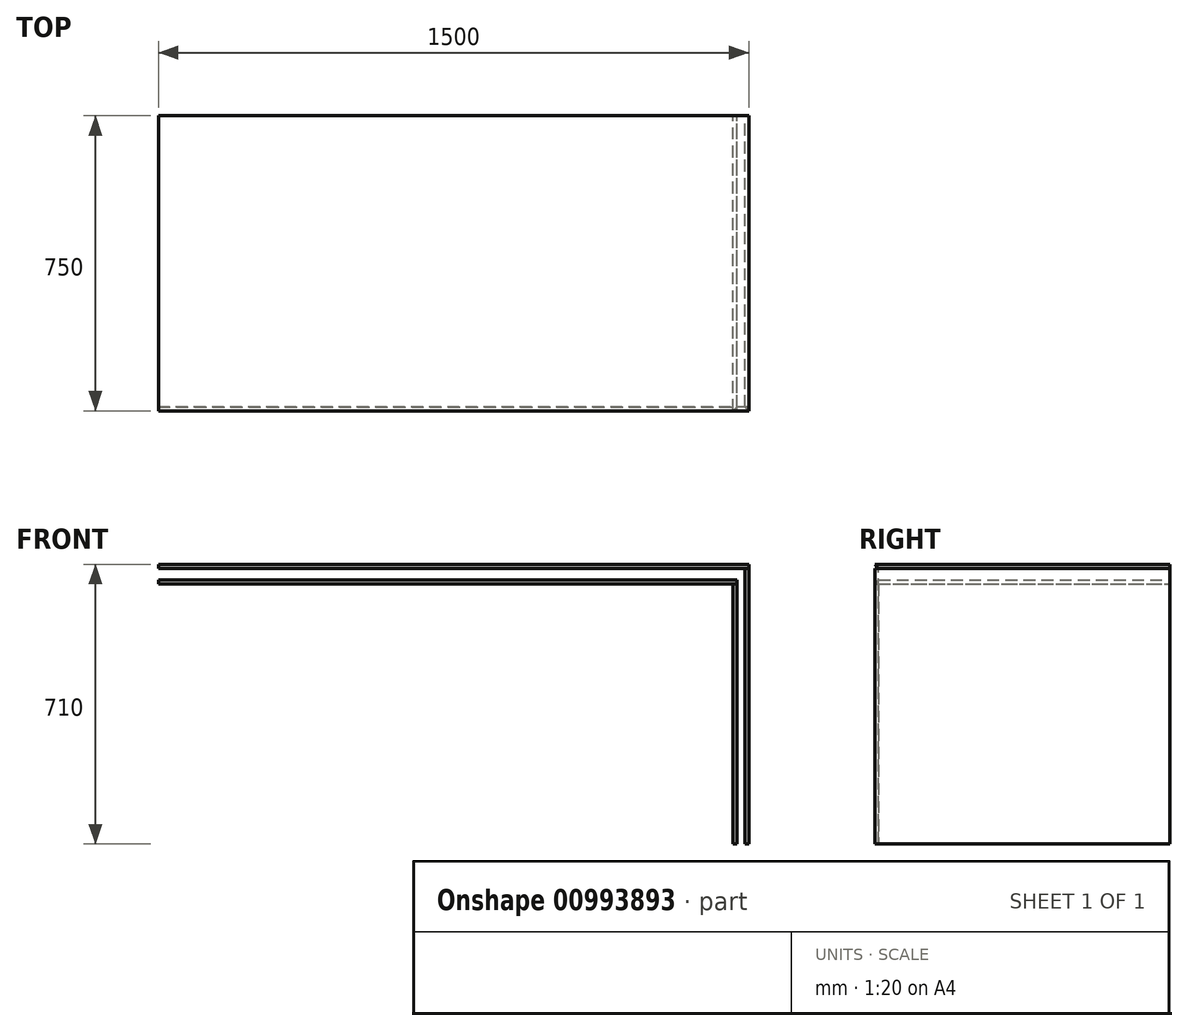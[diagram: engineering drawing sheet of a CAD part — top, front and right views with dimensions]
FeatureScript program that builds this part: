
annotation { "Feature Type Name" : "Feature", "Feature Type Description" : "" }
export const myFeature = defineFeature(function(context is Context, id is Id, definition is map)
    precondition{}
    {
        {
            assignVariable(context, id + "F0", {"name" : "t_board_thickness", "anyValue" : 10});
        }
        {
            assignVariable(context, id + "F1", {"name" : "t_depth", "anyValue" : 750});
        }
        {
            var Q0;
            Q0=qCreatedBy(makeId("Front.planeOp"),FACE);
            var sketch = newSketch(context, id + "F2", { "sketchPlane" : qUnion([Q0])});
            skLineSegment(sketch, "E0.bottom", {"start": v(-1265, 2470) * mm, "end": v(1265, 2470) * mm});
            skLineSegment(sketch, "E0.top", {"start": v(-1265, 0) * mm, "end": v(1265, 0) * mm});
            skLineSegment(sketch, "E0.left", {"start": v(-1265, 2470) * mm, "end": v(-1265, 0) * mm});
            skLineSegment(sketch, "E0.right", {"start": v(1265, 2470) * mm, "end": v(1265, 0) * mm});
            skSolve(sketch);
        }
        {
            var Q0;
            Q0=makeQuery(id+"F2.imprint","IMPRINT",FACE,{"disambiguationData":[TD([[makeQuery(id+"F2.imprint","IMPRINT",EDGE,{"derivedFrom":sQuery(id+"F2.wireOp",EDGE,"E0.bottom")}),-1.0]])]});
            var sketch = newSketch(context, id + "F3", { "sketchPlane" : qUnion([Q0])});
            skLineSegment(sketch, "E1.bottom", {"start": v(-1265, 710) * mm, "end": v(235, 710) * mm});
            skLineSegment(sketch, "E1.top", {"start": v(-1265, 700) * mm, "end": v(235, 700) * mm});
            skLineSegment(sketch, "E1.left", {"start": v(-1265, 710) * mm, "end": v(-1265, 700) * mm});
            skLineSegment(sketch, "E1.right", {"start": v(235, 710) * mm, "end": v(235, 700) * mm});
            skSolve(sketch);
        }
        {
            var Q0;
            Q0=makeQuery(id+"F2.imprint","IMPRINT",FACE,{"disambiguationData":[TD([[makeQuery(id+"F2.imprint","IMPRINT",EDGE,{"derivedFrom":sQuery(id+"F2.wireOp",EDGE,"E0.bottom")}),-1.0]])]});
            var sketch = newSketch(context, id + "F4", { "sketchPlane" : qUnion([Q0])});
            skLineSegment(sketch, "E2.bottom", {"start": v(-1265, 670) * mm, "end": v(205, 670) * mm});
            skLineSegment(sketch, "E2.top", {"start": v(-1265, 660) * mm, "end": v(205, 660) * mm});
            skLineSegment(sketch, "E2.left", {"start": v(-1265, 670) * mm, "end": v(-1265, 660) * mm});
            skLineSegment(sketch, "E2.right", {"start": v(205, 670) * mm, "end": v(205, 660) * mm});
            skSolve(sketch);
        }
        {
            var Q0;
            Q0=makeQuery(id+"F2.imprint","IMPRINT",FACE,{"disambiguationData":[TD([[makeQuery(id+"F2.imprint","IMPRINT",EDGE,{"derivedFrom":sQuery(id+"F2.wireOp",EDGE,"E0.bottom")}),-1.0]])]});
            var sketch = newSketch(context, id + "F5", { "sketchPlane" : qUnion([Q0])});
            skLineSegment(sketch, "E3.bottom", {"start": v(225, 700) * mm, "end": v(235, 700) * mm});
            skLineSegment(sketch, "E3.top", {"start": v(225, 0) * mm, "end": v(235, 0) * mm});
            skLineSegment(sketch, "E3.left", {"start": v(225, 700) * mm, "end": v(225, 0) * mm});
            skLineSegment(sketch, "E3.right", {"start": v(235, 700) * mm, "end": v(235, 0) * mm});
            skSolve(sketch);
        }
        {
            var Q0;
            Q0=makeQuery(id+"F2.imprint","IMPRINT",FACE,{"disambiguationData":[TD([[makeQuery(id+"F2.imprint","IMPRINT",EDGE,{"derivedFrom":sQuery(id+"F2.wireOp",EDGE,"E0.bottom")}),-1.0]])]});
            var sketch = newSketch(context, id + "F6", { "sketchPlane" : qUnion([Q0])});
            skLineSegment(sketch, "E4.bottom", {"start": v(195, 660) * mm, "end": v(205, 660) * mm});
            skLineSegment(sketch, "E4.top", {"start": v(195, 0) * mm, "end": v(205, 0) * mm});
            skLineSegment(sketch, "E4.left", {"start": v(195, 660) * mm, "end": v(195, 0) * mm});
            skLineSegment(sketch, "E4.right", {"start": v(205, 660) * mm, "end": v(205, 0) * mm});
            skSolve(sketch);
        }
        {
            var Q0;
            Q0 = qSketchRegion(id + "F3", true);
            var Q1;
            Q1 = qConstructionFilter(qBodyType(qCreatedBy(id + "F3" ,EDGE), BodyType.WIRE), ConstructionObject.NO);
            extrude(context, id + "F7", {"entities" : qUnion([Q0]), "surfaceEntities" : qUnion([Q1]), "depth" : (getVariable(context, 't_depth')) * mm, "offsetDistance" : 25 * mm});
        }
        {
            var Q0;
            Q0 = qSketchRegion(id + "F4", true);
            var Q1;
            Q1 = qConstructionFilter(qBodyType(qCreatedBy(id + "F4" ,EDGE), BodyType.WIRE), ConstructionObject.NO);
            extrude(context, id + "F8", {"entities" : qUnion([Q0]), "surfaceEntities" : qUnion([Q1]), "depth" : (getVariable(context, 't_depth')) * mm, "offsetDistance" : 25 * mm});
        }
        {
            var Q0;
            Q0 = qSketchRegion(id + "F5", true);
            extrude(context, id + "F9", {"entities" : qUnion([Q0]), "depth" : (getVariable(context, 't_depth')) * mm, "offsetDistance" : 25 * mm});
        }
        {
            var Q0;
            Q0 = qSketchRegion(id + "F6", true);
            var Q1;
            Q1 = qConstructionFilter(qBodyType(qCreatedBy(id + "F6" ,EDGE), BodyType.WIRE), ConstructionObject.NO);
            extrude(context, id + "F10", {"entities" : qUnion([Q0]), "surfaceEntities" : qUnion([Q1]), "depth" : (getVariable(context, 't_depth')) * mm, "offsetDistance" : 25 * mm});
        }
        {
            var Q0;
            Q0=makeQuery(id+"F7.opExtrude","CAP_EDGE",EDGE,{"disambiguationData":[OSD([sQuery(id+"F3.wireOp",EDGE,"E1.top")])],"isStart":false});
            chamfer(context, id + "F11", {"entities" : qUnion([Q0]), "width" : (getVariable(context, 't_board_thickness')) * mm, "tangentPropagation" : true});
        }
        {
            var Q0;
            Q0=makeQuery(id+"F8.opExtrude","CAP_EDGE",EDGE,{"disambiguationData":[OSD([sQuery(id+"F4.wireOp",EDGE,"E2.bottom")])],"isStart":false});
            chamfer(context, id + "F12", {"entities" : qUnion([Q0]), "width" : (getVariable(context, 't_board_thickness')) * mm, "tangentPropagation" : true});
        }
        {
            var Q0;
            Q0=makeQuery(id+"F10.opExtrude","CAP_EDGE",EDGE,{"disambiguationData":[OSD([sQuery(id+"F6.wireOp",EDGE,"E4.right")])],"isStart":false});
            chamfer(context, id + "F13", {"entities" : qUnion([Q0]), "width" : (getVariable(context, 't_board_thickness')) * mm, "tangentPropagation" : true});
        }
        {
            var Q0;
            Q0=makeQuery(id+"F9.opExtrude","CAP_EDGE",EDGE,{"disambiguationData":[OSD([sQuery(id+"F5.wireOp",EDGE,"E3.left")])],"isStart":false});
            chamfer(context, id + "F14", {"entities" : qUnion([Q0]), "width" : (getVariable(context, 't_board_thickness')) * mm, "tangentPropagation" : true});
        }
    });
